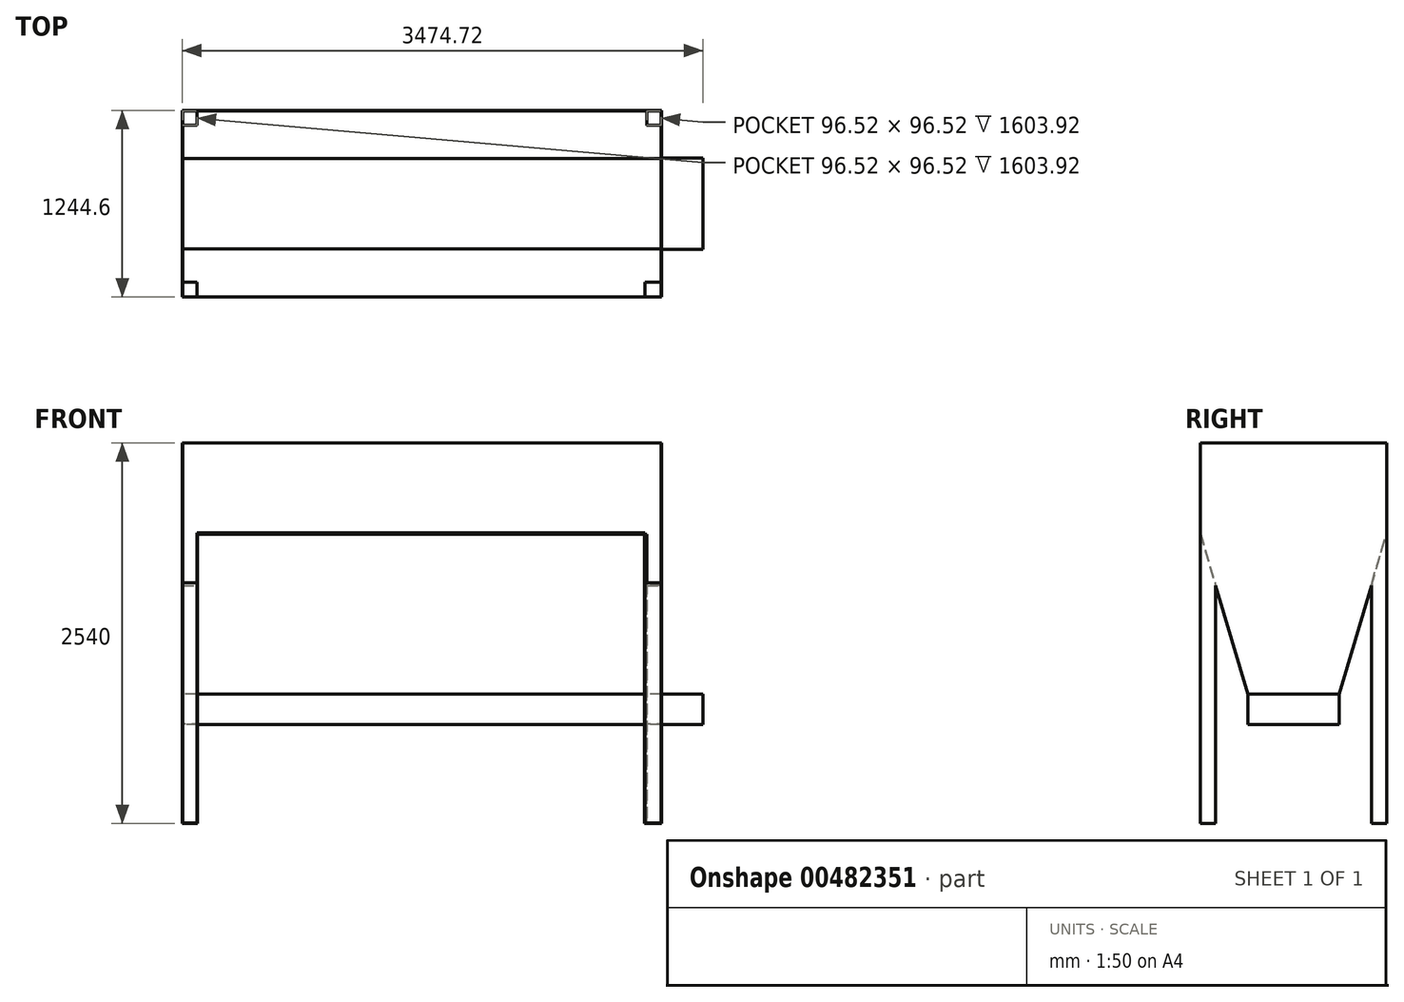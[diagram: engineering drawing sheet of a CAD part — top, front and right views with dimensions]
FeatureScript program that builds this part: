
annotation { "Feature Type Name" : "Feature", "Feature Type Description" : "" }
export const myFeature = defineFeature(function(context is Context, id is Id, definition is map)
    precondition{}
    {
        {
            var Q0;
            Q0=qCreatedBy(makeId("Right.planeOp"),FACE);
            var sketch = newSketch(context, id + "F0", { "sketchPlane" : qUnion([Q0])});
            skLineSegment(sketch, "E0", {"start": v(-304.8, 660.4) * mm, "end": v(-304.8, 863.6) * mm});
            skLineSegment(sketch, "E1", {"start": v(0, 660.4) * mm, "end": v(-304.8, 660.4) * mm});
            skLineSegment(sketch, "E2", {"start": v(-304.8, 863.6) * mm, "end": v(-622.3, 1930.4) * mm});
            skLineSegment(sketch, "E3", {"start": v(-622.3, 1930.4) * mm, "end": v(-622.3, 2540) * mm});
            skLineSegment(sketch, "E4", {"start": v(-622.3, 2540) * mm, "end": v(0, 2540) * mm});
            skLineSegment(sketch, "E5", {"start": v(0, 660.4) * mm, "end": v(0, 356.52) * mm, "construction": true});
            skLineSegment(sketch, "E6.MirrorCS", {"start": v(304.8, 660.4) * mm, "end": v(304.8, 863.6) * mm});
            skLineSegment(sketch, "E7.MirrorCS", {"start": v(0, 660.4) * mm, "end": v(304.8, 660.4) * mm});
            skLineSegment(sketch, "E8.MirrorCS", {"start": v(304.8, 863.6) * mm, "end": v(622.3, 1930.4) * mm});
            skLineSegment(sketch, "E9.MirrorCS", {"start": v(622.3, 2540) * mm, "end": v(0, 2540) * mm});
            skLineSegment(sketch, "E10.MirrorCS", {"start": v(622.3, 1930.4) * mm, "end": v(622.3, 2540) * mm});
            skSolve(sketch);
        }
        {
            var Q0;
            Q0 = qSketchRegion(id + "F0", true);
            extrude(context, id + "F1", {"entities" : qUnion([Q0]), "depth" : 3200.4 * mm, "offsetDistance" : 25.4 * mm});
        }
        {
            var Q0;
            Q0=qCreatedBy(makeId("Top.planeOp"),FACE);
            var sketch = newSketch(context, id + "F2", { "sketchPlane" : qUnion([Q0])});
            skLineSegment(sketch, "E11.bottom", {"start": v(3086.46, -520.7) * mm, "end": v(3200.4, -520.7) * mm});
            skLineSegment(sketch, "E11.top", {"start": v(3086.46, -622.3) * mm, "end": v(3200.4, -622.3) * mm});
            skLineSegment(sketch, "E11.left", {"start": v(3086.46, -520.7) * mm, "end": v(3086.46, -622.3) * mm});
            skLineSegment(sketch, "E11.right", {"start": v(3200.4, -520.7) * mm, "end": v(3200.4, -622.3) * mm});
            skLineSegment(sketch, "E12.bottom", {"start": v(3098.8, 520.7) * mm, "end": v(3200.4, 520.7) * mm});
            skLineSegment(sketch, "E12.top", {"start": v(3098.8, 622.3) * mm, "end": v(3200.4, 622.3) * mm});
            skLineSegment(sketch, "E12.left", {"start": v(3098.8, 520.7) * mm, "end": v(3098.8, 622.3) * mm});
            skLineSegment(sketch, "E12.right", {"start": v(3200.4, 520.7) * mm, "end": v(3200.4, 622.3) * mm});
            skLineSegment(sketch, "E13.bottom", {"start": v(101.6, 520.7) * mm, "end": v(0, 520.7) * mm});
            skLineSegment(sketch, "E13.top", {"start": v(101.6, 622.3) * mm, "end": v(0, 622.3) * mm});
            skLineSegment(sketch, "E13.left", {"start": v(101.6, 520.7) * mm, "end": v(101.6, 622.3) * mm});
            skLineSegment(sketch, "E13.right", {"start": v(0, 520.7) * mm, "end": v(0, 622.3) * mm});
            skLineSegment(sketch, "E14.bottom", {"start": v(101.6, -520.7) * mm, "end": v(0, -520.7) * mm});
            skLineSegment(sketch, "E14.top", {"start": v(101.6, -622.3) * mm, "end": v(0, -622.3) * mm});
            skLineSegment(sketch, "E14.left", {"start": v(101.6, -520.7) * mm, "end": v(101.6, -622.3) * mm});
            skLineSegment(sketch, "E14.right", {"start": v(0, -520.7) * mm, "end": v(0, -622.3) * mm});
            skSolve(sketch);
        }
        {
            var Q0;
            Q0 = qSketchRegion(id + "F2", true);
            extrude(context, id + "F3", {"entities" : qUnion([Q0]), "operationType" : NewBodyOperationType.ADD, "endBound" : BoundingType.UP_TO_NEXT, "depth" : 25.4 * mm, "offsetDistance" : 25.4 * mm});
        }
        {
            var Q0;
            Q0=makeQuery(id+"F3.boolean.opBoolean","MERGE",FACE,{"derivedFrom":[makeQuery(id+"F1.opExtrude","CAP_FACE",FACE,{"disambiguationData":[OSD([sQuery(id+"F0.wireOp",EDGE,"E0"),sQuery(id+"F0.wireOp",EDGE,"E1"),sQuery(id+"F0.wireOp",EDGE,"E2"),sQuery(id+"F0.wireOp",EDGE,"E3"),sQuery(id+"F0.wireOp",EDGE,"E4"),sQuery(id+"F0.wireOp",EDGE,"E6.MirrorCS"),sQuery(id+"F0.wireOp",EDGE,"E7.MirrorCS"),sQuery(id+"F0.wireOp",EDGE,"E8.MirrorCS"),sQuery(id+"F0.wireOp",EDGE,"E9.MirrorCS"),sQuery(id+"F0.wireOp",EDGE,"E10.MirrorCS")])],"isStart":false}),makeQuery(id+"F3.opExtrude","SWEPT_FACE",FACE,{"disambiguationData":[OSD([sQuery(id+"F2.wireOp",EDGE,"E11.right")])]}),makeQuery(id+"F3.opExtrude","SWEPT_FACE",FACE,{"disambiguationData":[OSD([sQuery(id+"F2.wireOp",EDGE,"E12.right")])]})]});
            var sketch = newSketch(context, id + "F4", { "sketchPlane" : qUnion([Q0])});
            skLineSegment(sketch, "E15.bottom", {"start": v(-304.8, 660.4) * mm, "end": v(304.8, 660.4) * mm});
            skLineSegment(sketch, "E15.top", {"start": v(-304.8, 863.6) * mm, "end": v(304.8, 863.6) * mm});
            skLineSegment(sketch, "E15.left", {"start": v(-304.8, 660.4) * mm, "end": v(-304.8, 863.6) * mm});
            skLineSegment(sketch, "E15.right", {"start": v(304.8, 660.4) * mm, "end": v(304.8, 863.6) * mm});
            skSolve(sketch);
        }
        {
            var Q0;
            Q0 = qSketchRegion(id + "F4", true);
            extrude(context, id + "F5", {"entities" : qUnion([Q0]), "operationType" : NewBodyOperationType.ADD, "depth" : 274.32 * mm, "offsetDistance" : 25.4 * mm});
        }
        {
            var Q0;
            Q0=makeQuery(id+"F1.opExtrude","SWEPT_FACE",FACE,{"disambiguationData":[OSD([sQuery(id+"F0.wireOp",EDGE,"E4"),sQuery(id+"F0.wireOp",EDGE,"E9.MirrorCS")])]});
            var Q1;
            Q1=makeQuery(id+"F3.boolean.opBoolean","MERGE",FACE,{"derivedFrom":[makeQuery(id+"F1.opExtrude","SWEPT_FACE",FACE,{"disambiguationData":[OSD([sQuery(id+"F0.wireOp",EDGE,"E3")])]}),makeQuery(id+"F3.opExtrude","SWEPT_FACE",FACE,{"disambiguationData":[OSD([sQuery(id+"F2.wireOp",EDGE,"E11.top")])]}),makeQuery(id+"F3.opExtrude","SWEPT_FACE",FACE,{"disambiguationData":[OSD([sQuery(id+"F2.wireOp",EDGE,"E14.top")])]})]});
            shell(context, id + "F6", {"entities" : qUnion([Q0, Q1]), "thickness" : 2.54 * mm});
        }
    });
